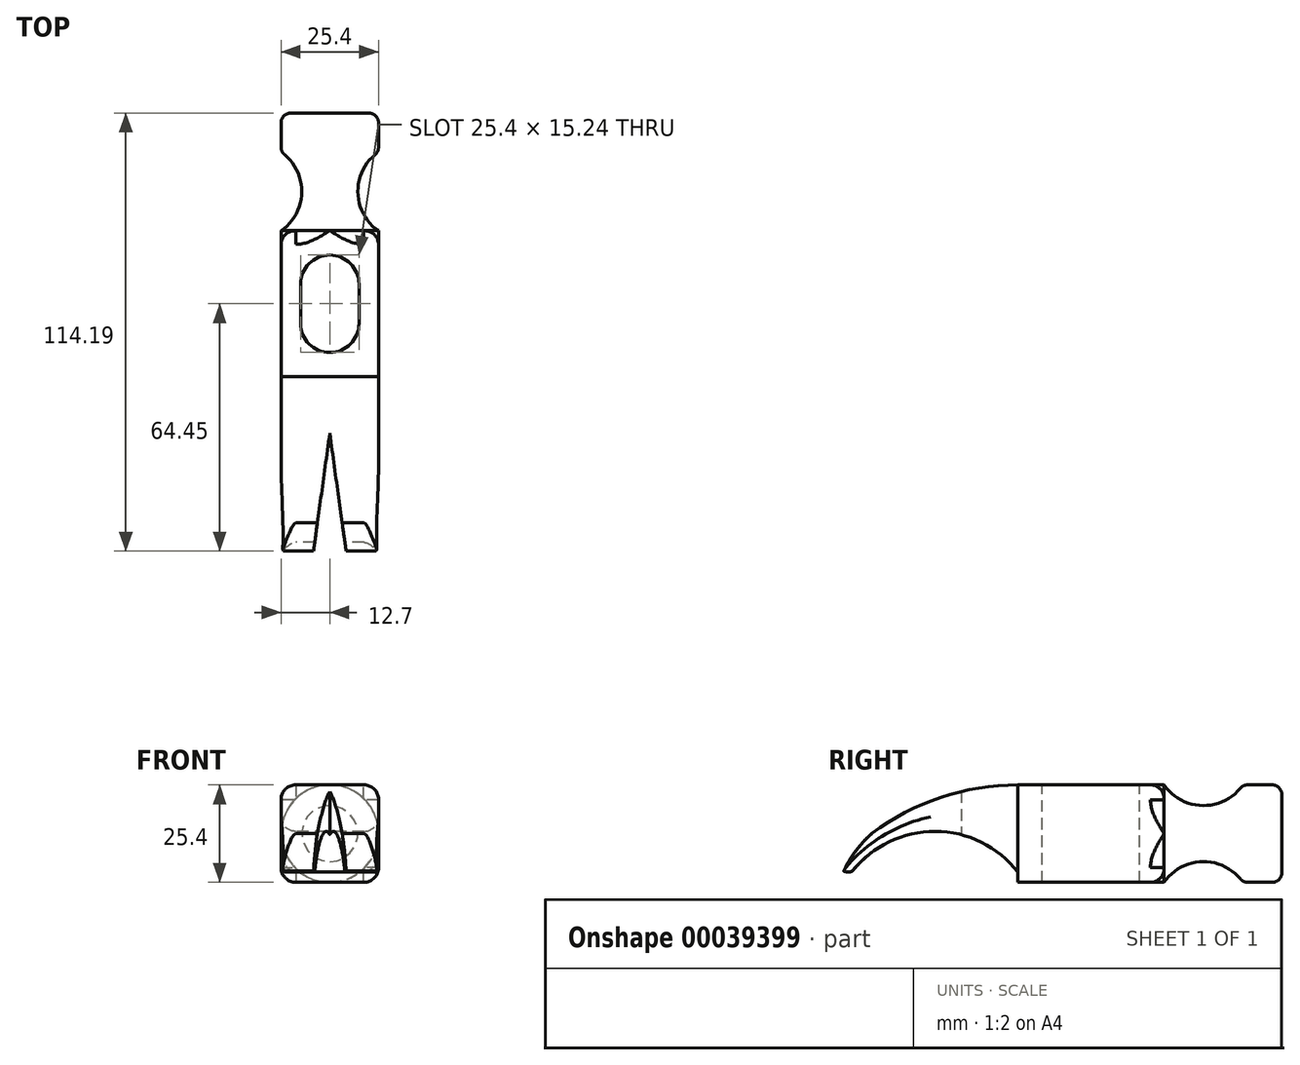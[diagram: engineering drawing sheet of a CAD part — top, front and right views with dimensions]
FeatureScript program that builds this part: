
annotation { "Feature Type Name" : "Feature", "Feature Type Description" : "" }
export const myFeature = defineFeature(function(context is Context, id is Id, definition is map)
    precondition{}
    {
        {
            var Q0;
            Q0=qCreatedBy(makeId("Front.planeOp"),FACE);
            var sketch = newSketch(context, id + "F0", { "sketchPlane" : qUnion([Q0])});
            skLineSegment(sketch, "E0", {"start": v(0, 0) * mm, "end": v(0, 12.7) * mm, "construction": true});
            skLineSegment(sketch, "E1", {"start": v(0, 0) * mm, "end": v(12.7, 0) * mm, "construction": true});
            skLineSegment(sketch, "E2", {"start": v(0, 12.7) * mm, "end": v(12.7, 12.7) * mm});
            skLineSegment(sketch, "E3", {"start": v(12.7, 12.7) * mm, "end": v(12.7, 0) * mm});
            skLineSegment(sketch, "E4", {"start": v(12.7, 0) * mm, "end": v(12.7, -12.7) * mm});
            skLineSegment(sketch, "E5", {"start": v(12.7, -12.7) * mm, "end": v(-12.7, -12.7) * mm});
            skLineSegment(sketch, "E6", {"start": v(-12.7, -12.7) * mm, "end": v(-12.7, 12.7) * mm});
            skLineSegment(sketch, "E7", {"start": v(-12.7, 12.7) * mm, "end": v(0, 12.7) * mm});
            skSolve(sketch);
        }
        {
            var Q0;
            Q0 = qSketchRegion(id + "F0", true);
            extrude(context, id + "F1", {"entities" : qUnion([Q0]), "depth" : 38.1 * mm});
        }
        {
            var Q0;
            Q0=qCreatedBy(makeId("Top.planeOp"),FACE);
            var sketch = newSketch(context, id + "F2", { "sketchPlane" : qUnion([Q0])});
            skLineSegment(sketch, "E8", {"start": v(0, 20.53) * mm, "end": v(0, 0) * mm});
            skLineSegment(sketch, "E9", {"start": v(0, 0) * mm, "end": v(-12.7, 0) * mm});
            skLineSegment(sketch, "E10", {"start": v(-12.7, 20.53) * mm, "end": v(-12.7, 30.7) * mm});
            skLineSegment(sketch, "E11", {"start": v(-12.7, 30.7) * mm, "end": v(0, 30.7) * mm});
            skArc(sketch, "E12", {"start": v(-12.7, 0) * mm, "mid": v(-7.3, 10.27) * mm, "end": v(-12.7, 20.53) * mm});
            skLineSegment(sketch, "E13", {"start": v(0, 30.7) * mm, "end": v(0, 20.53) * mm});
            skSolve(sketch);
        }
        {
            var Q0;
            Q0=makeQuery(id+"F2.imprint","IMPRINT",FACE,{"disambiguationData":[TD([[makeQuery(id+"F2.imprint","IMPRINT",EDGE,{"derivedFrom":sQuery(id+"F2.wireOp",EDGE,"E8")}),-1.0]])]});
            var Q1;
            Q1=sQuery(id+"F2.wireOp",EDGE,"E13");
            revolve(context, id + "F3", {"operationType" : NewBodyOperationType.ADD, "entities" : qUnion([Q0]), "axis" : qUnion([Q1]), "revolveType" : RevolveType.FULL});
        }
        {
            var Q0;
            Q0=makeQuery(id+"F3.opRevolve","SWEPT_EDGE",EDGE,{"disambiguationData":[OSD([sQuery(id+"F2.wireOp",EDGE,"E10"),sQuery(id+"F2.wireOp",EDGE,"E11")])]});
            var Q1;
            Q1=makeQuery(id+"F3.opRevolve","SWEPT_EDGE",EDGE,{"disambiguationData":[OSD([sQuery(id+"F2.wireOp",EDGE,"E10"),sQuery(id+"F2.wireOp",EDGE,"E12")])]});
            fillet(context, id + "F4", {"entities" : qUnion([Q0, Q1]), "radius" : 2.54 * mm, "tangentPropagation" : true, "allowEdgeOverflow" : false});
        }
        {
            var Q0;
            Q0=makeQuery(id+"F1.opExtrude","SWEPT_FACE",FACE,{"disambiguationData":[OSD([sQuery(id+"F0.wireOp",EDGE,"E6")])]});
            var sketch = newSketch(context, id + "F5", { "sketchPlane" : qUnion([Q0])});
            skLineSegment(sketch, "E14", {"start": v(38.1, 0) * mm, "end": v(76.2, 0) * mm, "construction": true});
            skPoint(sketch, "E14.endSnap0", {"position": v(38.1, 0) * mm});
            skArc(sketch, "E15", {"start": v(76.2, 0) * mm, "mid": v(58.18, 9.44) * mm, "end": v(38.1, 12.7) * mm});
            skLineSegment(sketch, "E16", {"start": v(76.2, 0) * mm, "end": v(76.2, -7.62) * mm});
            skLineSegment(sketch, "E17", {"start": v(38.1, 12.7) * mm, "end": v(38.1, -12.7) * mm});
            skArc(sketch, "E18", {"start": v(83.5, -9.8) * mm, "mid": v(80.38, -4.5) * mm, "end": v(76.2, 0) * mm});
            skArc(sketch, "E19", {"start": v(81.27, -9.8) * mm, "mid": v(82.38, -10.01) * mm, "end": v(83.5, -9.8) * mm});
            skArc(sketch, "E20", {"start": v(81.27, -9.8) * mm, "mid": v(59.63, 0.58) * mm, "end": v(38.1, -10.02) * mm});
            skSolve(sketch);
        }
        {
            var Q0;
            Q0 = qSketchRegion(id + "F5", true);
            extrude(context, id + "F6", {"entities" : qUnion([Q0]), "oppositeDirection" : true, "depth" : 25.4 * mm});
        }
        {
            var Q0;
            Q0=qCreatedBy(makeId("Top.planeOp"),FACE);
            var sketch = newSketch(context, id + "F7", { "sketchPlane" : qUnion([Q0])});
            skLineSegment(sketch, "E21", {"start": v(0, -85.85) * mm, "end": v(4.57, -85.85) * mm});
            skLineSegment(sketch, "E22", {"start": v(4.57, -85.85) * mm, "end": v(4.57, -52.83) * mm, "construction": true});
            skLineSegment(sketch, "E23", {"start": v(0, -85.85) * mm, "end": v(-4.57, -85.85) * mm});
            skLineSegment(sketch, "E24", {"start": v(-4.57, -85.85) * mm, "end": v(-4.57, -52.83) * mm, "construction": true});
            skLineSegment(sketch, "E25", {"start": v(-4.57, -52.83) * mm, "end": v(4.57, -52.83) * mm, "construction": true});
            skLineSegment(sketch, "E26", {"start": v(-4.57, -85.85) * mm, "end": v(0, -52.83) * mm});
            skLineSegment(sketch, "E27", {"start": v(0, -52.83) * mm, "end": v(4.57, -85.85) * mm});
            skSolve(sketch);
        }
        {
            var Q0;
            Q0 = qSketchRegion(id + "F7", true);
            extrude(context, id + "F8", {"entities" : qUnion([Q0]), "operationType" : NewBodyOperationType.REMOVE, "depth" : 25.4 * mm});
        }
        {
            var Q0;
            Q0=makeQuery(id+"F1.opExtrude","SWEPT_EDGE",EDGE,{"disambiguationData":[OSD([sQuery(id+"F0.wireOp",EDGE,"E6"),sQuery(id+"F0.wireOp",EDGE,"E7")])]});
            var Q1;
            Q1=makeQuery(id+"F1.opExtrude","SWEPT_EDGE",EDGE,{"disambiguationData":[OSD([sQuery(id+"F0.wireOp",EDGE,"E2"),sQuery(id+"F0.wireOp",EDGE,"E3")])]});
            var Q2;
            Q2=makeQuery(id+"F6.opExtrude","CAP_EDGE",EDGE,{"disambiguationData":[OSD([sQuery(id+"F5.wireOp",EDGE,"E15")])],"isStart":true});
            var Q3;
            Q3=makeQuery(id+"F6.opExtrude","CAP_EDGE",EDGE,{"disambiguationData":[OSD([sQuery(id+"F5.wireOp",EDGE,"E15")])],"isStart":false});
            var Q4;
            Q4=makeQuery(id+"F6.opExtrude","CAP_EDGE",EDGE,{"disambiguationData":[OSD([sQuery(id+"F5.wireOp",EDGE,"E20")])],"isStart":true});
            var Q5;
            Q5=makeQuery(id+"F6.opExtrude","CAP_EDGE",EDGE,{"disambiguationData":[OSD([sQuery(id+"F5.wireOp",EDGE,"E20")])],"isStart":false});
            var Q6;
            Q6=makeQuery(id+"F1.opExtrude","SWEPT_EDGE",EDGE,{"disambiguationData":[OSD([sQuery(id+"F0.wireOp",EDGE,"E4"),sQuery(id+"F0.wireOp",EDGE,"E5")])]});
            var Q7;
            Q7=makeQuery(id+"F1.opExtrude","SWEPT_EDGE",EDGE,{"disambiguationData":[OSD([sQuery(id+"F0.wireOp",EDGE,"E5"),sQuery(id+"F0.wireOp",EDGE,"E6")])]});
            fillet(context, id + "F9", {"entities" : qUnion([Q0, Q1, Q2, Q3, Q4, Q5, Q6, Q7]), "radius" : 3.8 * mm, "tangentPropagation" : true, "allowEdgeOverflow" : false});
        }
        {
            var Q0;
            {var subQ0=sQuery(id+"F7.wireOp",EDGE,"E26");var subQ1=sQuery(id+"F7.wireOp",EDGE,"E27");Q0=makeQuery(id+"F8.boolean.opBoolean","COPY",FACE,{"disambiguationData":[TD([makeQuery(id+"F6.opExtrude","SWEPT_FACE",FACE,{"disambiguationData":[OSD([sQuery(id+"F5.wireOp",EDGE,"E15")])]}),makeQuery(id+"F6.opExtrude","SWEPT_FACE",FACE,{"disambiguationData":[OSD([sQuery(id+"F5.wireOp",EDGE,"E18")])]}),makeQuery(id+"F6.opExtrude","SWEPT_FACE",FACE,{"disambiguationData":[OSD([sQuery(id+"F5.wireOp",EDGE,"E20")])]}),makeQuery(id+"F8.opExtrude","SWEPT_FACE",FACE,{"disambiguationData":[OSD([subQ0])]}),makeQuery(id+"F8.opExtrude","SWEPT_FACE",FACE,{"disambiguationData":[OSD([subQ1])]})])],"derivedFrom":makeQuery(id+"F8.opExtrude","CAP_FACE",FACE,{"disambiguationData":[OSD([sQuery(id+"F7.wireOp",EDGE,"E21"),sQuery(id+"F7.wireOp",EDGE,"E23"),subQ0,subQ1])],"isStart":true})});}
            var sketch = newSketch(context, id + "F10", { "sketchPlane" : qUnion([Q0])});
            skLineSegment(sketch, "E28", {"start": v(-1.74, -65.38) * mm, "end": v(-3.24, -76.2) * mm});
            skLineSegment(sketch, "E29", {"start": v(1.74, -65.38) * mm, "end": v(3.24, -76.2) * mm});
            skLineSegment(sketch, "E30", {"start": v(0, -52.83) * mm, "end": v(-3.54, -78.42) * mm});
            skLineSegment(sketch, "E31", {"start": v(-3.54, -78.42) * mm, "end": v(-5.25, -90.78) * mm});
            skLineSegment(sketch, "E32", {"start": v(0, -52.83) * mm, "end": v(4.52, -85.47) * mm});
            skLineSegment(sketch, "E33", {"start": v(4.52, -85.47) * mm, "end": v(-4.52, -85.47) * mm});
            skSolve(sketch);
        }
        {
            var Q0;
            Q0 = qSketchRegion(id + "F10", true);
            extrude(context, id + "F11", {"entities" : qUnion([Q0]), "operationType" : NewBodyOperationType.REMOVE, "oppositeDirection" : true, "depth" : 25.4 * mm});
        }
        {
            var Q0;
            {var subQ0=sQuery(id+"F0.wireOp",EDGE,"E5");var subQ1=sQuery(id+"F0.wireOp",EDGE,"E4");var subQ2=sQuery(id+"F0.wireOp",EDGE,"E3");var subQ3=makeQuery(id+"F1.opExtrude","CAP_FACE",FACE,{"disambiguationData":[OSD([sQuery(id+"F0.wireOp",EDGE,"E2"),subQ2,subQ1,subQ0,sQuery(id+"F0.wireOp",EDGE,"E6"),sQuery(id+"F0.wireOp",EDGE,"E7")])],"isStart":true});Q0=makeQuery(id+"F9.opFillet","BLEND_EDGE",EDGE,{"blendedFrom":[makeQuery(id+"F1.opExtrude","SWEPT_EDGE",EDGE,{"disambiguationData":[OSD([subQ1,subQ0])]}),makeQuery(id+"F3.boolean.opBoolean","SPLIT",FACE,{"disambiguationData":[TD([subQ3,makeQuery(id+"F1.opExtrude","SWEPT_FACE",FACE,{"disambiguationData":[OSD([subQ2,subQ1])]}),makeQuery(id+"F1.opExtrude","SWEPT_FACE",FACE,{"disambiguationData":[OSD([subQ0])]}),makeQuery(id+"F3.opRevolve","SWEPT_FACE",FACE,{"disambiguationData":[OSD([sQuery(id+"F2.wireOp",EDGE,"E12")])]})])],"derivedFrom":subQ3})],"blendedInto":[makeQuery(id+"F3.boolean.opBoolean","SPLIT",FACE,{"disambiguationData":[TD([subQ3,makeQuery(id+"F1.opExtrude","SWEPT_FACE",FACE,{"disambiguationData":[OSD([subQ2,subQ1])]}),makeQuery(id+"F1.opExtrude","SWEPT_FACE",FACE,{"disambiguationData":[OSD([subQ0])]}),makeQuery(id+"F3.opRevolve","SWEPT_FACE",FACE,{"disambiguationData":[OSD([sQuery(id+"F2.wireOp",EDGE,"E12")])]})])],"derivedFrom":subQ3})]});}
            var Q1;
            {var subQ0=sQuery(id+"F0.wireOp",EDGE,"E7");var subQ1=sQuery(id+"F0.wireOp",EDGE,"E4");var subQ2=sQuery(id+"F0.wireOp",EDGE,"E3");var subQ3=sQuery(id+"F0.wireOp",EDGE,"E2");var subQ4=makeQuery(id+"F1.opExtrude","CAP_FACE",FACE,{"disambiguationData":[OSD([subQ3,subQ2,subQ1,sQuery(id+"F0.wireOp",EDGE,"E5"),sQuery(id+"F0.wireOp",EDGE,"E6"),subQ0])],"isStart":true});Q1=makeQuery(id+"F9.opFillet","BLEND_EDGE",EDGE,{"blendedFrom":[makeQuery(id+"F1.opExtrude","SWEPT_EDGE",EDGE,{"disambiguationData":[OSD([subQ3,subQ2])]}),makeQuery(id+"F3.boolean.opBoolean","SPLIT",FACE,{"disambiguationData":[TD([subQ4,makeQuery(id+"F1.opExtrude","SWEPT_FACE",FACE,{"disambiguationData":[OSD([subQ3,subQ0])]}),makeQuery(id+"F1.opExtrude","SWEPT_FACE",FACE,{"disambiguationData":[OSD([subQ2,subQ1])]}),makeQuery(id+"F3.opRevolve","SWEPT_FACE",FACE,{"disambiguationData":[OSD([sQuery(id+"F2.wireOp",EDGE,"E12")])]})])],"derivedFrom":subQ4})],"blendedInto":[makeQuery(id+"F3.boolean.opBoolean","SPLIT",FACE,{"disambiguationData":[TD([subQ4,makeQuery(id+"F1.opExtrude","SWEPT_FACE",FACE,{"disambiguationData":[OSD([subQ3,subQ0])]}),makeQuery(id+"F1.opExtrude","SWEPT_FACE",FACE,{"disambiguationData":[OSD([subQ2,subQ1])]}),makeQuery(id+"F3.opRevolve","SWEPT_FACE",FACE,{"disambiguationData":[OSD([sQuery(id+"F2.wireOp",EDGE,"E12")])]})])],"derivedFrom":subQ4})]});}
            var Q2;
            {var subQ0=sQuery(id+"F0.wireOp",EDGE,"E6");var subQ1=sQuery(id+"F0.wireOp",EDGE,"E5");var subQ2=makeQuery(id+"F1.opExtrude","CAP_FACE",FACE,{"disambiguationData":[OSD([sQuery(id+"F0.wireOp",EDGE,"E2"),sQuery(id+"F0.wireOp",EDGE,"E3"),sQuery(id+"F0.wireOp",EDGE,"E4"),subQ1,subQ0,sQuery(id+"F0.wireOp",EDGE,"E7")])],"isStart":true});Q2=makeQuery(id+"F9.opFillet","BLEND_EDGE",EDGE,{"blendedFrom":[makeQuery(id+"F1.opExtrude","SWEPT_EDGE",EDGE,{"disambiguationData":[OSD([subQ1,subQ0])]}),makeQuery(id+"F3.boolean.opBoolean","SPLIT",FACE,{"disambiguationData":[TD([subQ2,makeQuery(id+"F1.opExtrude","SWEPT_FACE",FACE,{"disambiguationData":[OSD([subQ1])]}),makeQuery(id+"F1.opExtrude","SWEPT_FACE",FACE,{"disambiguationData":[OSD([subQ0])]}),makeQuery(id+"F3.opRevolve","SWEPT_FACE",FACE,{"disambiguationData":[OSD([sQuery(id+"F2.wireOp",EDGE,"E12")])]})])],"derivedFrom":subQ2})],"blendedInto":[makeQuery(id+"F3.boolean.opBoolean","SPLIT",FACE,{"disambiguationData":[TD([subQ2,makeQuery(id+"F1.opExtrude","SWEPT_FACE",FACE,{"disambiguationData":[OSD([subQ1])]}),makeQuery(id+"F1.opExtrude","SWEPT_FACE",FACE,{"disambiguationData":[OSD([subQ0])]}),makeQuery(id+"F3.opRevolve","SWEPT_FACE",FACE,{"disambiguationData":[OSD([sQuery(id+"F2.wireOp",EDGE,"E12")])]})])],"derivedFrom":subQ2})]});}
            var Q3;
            {var subQ0=sQuery(id+"F0.wireOp",EDGE,"E7");var subQ1=sQuery(id+"F0.wireOp",EDGE,"E6");var subQ2=sQuery(id+"F0.wireOp",EDGE,"E2");var subQ3=makeQuery(id+"F1.opExtrude","CAP_FACE",FACE,{"disambiguationData":[OSD([subQ2,sQuery(id+"F0.wireOp",EDGE,"E3"),sQuery(id+"F0.wireOp",EDGE,"E4"),sQuery(id+"F0.wireOp",EDGE,"E5"),subQ1,subQ0])],"isStart":true});Q3=makeQuery(id+"F9.opFillet","BLEND_EDGE",EDGE,{"blendedFrom":[makeQuery(id+"F1.opExtrude","SWEPT_EDGE",EDGE,{"disambiguationData":[OSD([subQ1,subQ0])]}),makeQuery(id+"F3.boolean.opBoolean","SPLIT",FACE,{"disambiguationData":[TD([subQ3,makeQuery(id+"F1.opExtrude","SWEPT_FACE",FACE,{"disambiguationData":[OSD([subQ2,subQ0])]}),makeQuery(id+"F1.opExtrude","SWEPT_FACE",FACE,{"disambiguationData":[OSD([subQ1])]}),makeQuery(id+"F3.opRevolve","SWEPT_FACE",FACE,{"disambiguationData":[OSD([sQuery(id+"F2.wireOp",EDGE,"E12")])]})])],"derivedFrom":subQ3})],"blendedInto":[makeQuery(id+"F3.boolean.opBoolean","SPLIT",FACE,{"disambiguationData":[TD([subQ3,makeQuery(id+"F1.opExtrude","SWEPT_FACE",FACE,{"disambiguationData":[OSD([subQ2,subQ0])]}),makeQuery(id+"F1.opExtrude","SWEPT_FACE",FACE,{"disambiguationData":[OSD([subQ1])]}),makeQuery(id+"F3.opRevolve","SWEPT_FACE",FACE,{"disambiguationData":[OSD([sQuery(id+"F2.wireOp",EDGE,"E12")])]})])],"derivedFrom":subQ3})]});}
            fillet(context, id + "F12", {"entities" : qUnion([Q0, Q1, Q2, Q3]), "radius" : 3.56 * mm, "tangentPropagation" : true, "allowEdgeOverflow" : false});
        }
        {
            var Q0;
            Q0=makeQuery(id+"F1.opExtrude","SWEPT_FACE",FACE,{"disambiguationData":[OSD([sQuery(id+"F0.wireOp",EDGE,"E2"),sQuery(id+"F0.wireOp",EDGE,"E7")])]});
            var sketch = newSketch(context, id + "F13", { "sketchPlane" : qUnion([Q0])});
            skLineSegment(sketch, "E34", {"start": v(0, 0) * mm, "end": v(0, -38.1) * mm, "construction": true});
            skLineSegment(sketch, "E35", {"start": v(-7.62, -13.97) * mm, "end": v(-7.62, -24.13) * mm});
            skLineSegment(sketch, "E36", {"start": v(7.62, -13.97) * mm, "end": v(7.62, -24.13) * mm});
            skLineSegment(sketch, "E37", {"start": v(-7.62, -13.97) * mm, "end": v(7.62, -13.97) * mm, "construction": true});
            skLineSegment(sketch, "E38", {"start": v(-7.62, -24.13) * mm, "end": v(7.62, -24.13) * mm, "construction": true});
            skLineSegment(sketch, "E39", {"start": v(-7.62, -19.05) * mm, "end": v(0, -19.05) * mm, "construction": true});
            skLineSegment(sketch, "E40", {"start": v(0, -19.05) * mm, "end": v(7.62, -19.05) * mm, "construction": true});
            skArc(sketch, "E41", {"start": v(7.62, -13.97) * mm, "mid": v(0, -6.35) * mm, "end": v(-7.62, -13.97) * mm});
            skArc(sketch, "E42", {"start": v(-7.62, -24.13) * mm, "mid": v(0, -31.75) * mm, "end": v(7.62, -24.13) * mm});
            skSolve(sketch);
        }
        {
            var Q0;
            Q0 = qSketchRegion(id + "F13", true);
            extrude(context, id + "F14", {"entities" : qUnion([Q0]), "operationType" : NewBodyOperationType.REMOVE, "oppositeDirection" : true, "depth" : 39.7 * mm});
        }
    });
